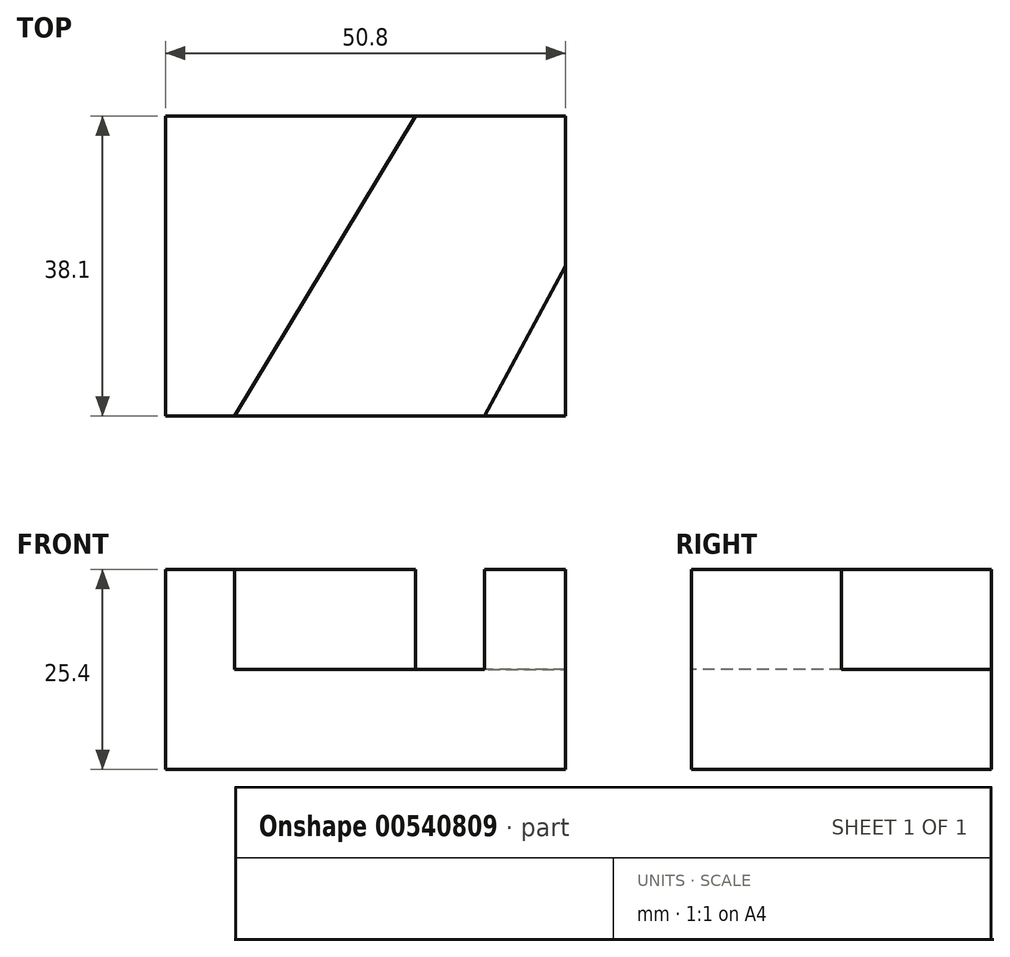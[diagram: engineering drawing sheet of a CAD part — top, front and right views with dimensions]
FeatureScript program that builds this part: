
annotation { "Feature Type Name" : "Feature", "Feature Type Description" : "" }
export const myFeature = defineFeature(function(context is Context, id is Id, definition is map)
    precondition{}
    {
        {
            var Q0;
            Q0=qCreatedBy(makeId("Front.planeOp"),FACE);
            var sketch = newSketch(context, id + "F0", { "sketchPlane" : qUnion([Q0])});
            skLineSegment(sketch, "E0", {"start": v(0, 0) * mm, "end": v(0, 25.4) * mm});
            skLineSegment(sketch, "E1", {"start": v(0, 25.4) * mm, "end": v(50.8, 25.4) * mm});
            skLineSegment(sketch, "E2", {"start": v(50.8, 25.4) * mm, "end": v(50.8, 0) * mm});
            skLineSegment(sketch, "E3", {"start": v(50.8, 0) * mm, "end": v(0, 0) * mm});
            skSolve(sketch);
        }
        {
            var Q0;
            Q0=makeQuery(id+"F0.imprint","IMPRINT",FACE,{"disambiguationData":[TD([[makeQuery(id+"F0.imprint","IMPRINT",EDGE,{"derivedFrom":sQuery(id+"F0.wireOp",EDGE,"E0")}),-1.0]])]});
            extrude(context, id + "F1", {"entities" : qUnion([Q0]), "depth" : 38.1 * mm, "offsetDistance" : 25.4 * mm});
        }
        {
            var Q0;
            Q0=makeQuery(id+"F1.opExtrude","SWEPT_FACE",FACE,{"disambiguationData":[OSD([sQuery(id+"F0.wireOp",EDGE,"E1")])]});
            var sketch = newSketch(context, id + "F2", { "sketchPlane" : qUnion([Q0])});
            skLineSegment(sketch, "E4", {"start": v(50.8, -19.05) * mm, "end": v(40.52, -38.1) * mm});
            skLineSegment(sketch, "E5", {"start": v(40.52, -38.1) * mm, "end": v(50.8, -38.1) * mm});
            skLineSegment(sketch, "E6", {"start": v(50.8, -38.1) * mm, "end": v(50.8, -19.05) * mm});
            skSolve(sketch);
        }
        {
            var Q0;
            {var subQ3=sQuery(id+"F2.wireOp",EDGE,"E4");Q0=makeQuery(id+"F2.imprint","IMPRINT",FACE,{"disambiguationData":[TD([[makeQuery(id+"F2.imprint","IMPRINT",EDGE,{"derivedFrom":subQ3}),-1.0]])]});}
            var sketch = newSketch(context, id + "F3", { "sketchPlane" : qUnion([Q0])});
            skLineSegment(sketch, "E7", {"start": v(31.75, 0) * mm, "end": v(8.77, -38.1) * mm});
            skLineSegment(sketch, "E8", {"start": v(8.77, -38.1) * mm, "end": v(40.52, -38.1) * mm});
            skLineSegment(sketch, "E9", {"start": v(40.52, -38.1) * mm, "end": v(50.8, -19.05) * mm});
            skLineSegment(sketch, "E10", {"start": v(50.8, -19.05) * mm, "end": v(50.8, 0) * mm});
            skLineSegment(sketch, "E11", {"start": v(50.8, 0) * mm, "end": v(31.75, 0) * mm});
            skSolve(sketch);
        }
        {
            var Q0;
            Q0=makeQuery(id+"F3.imprint","IMPRINT",FACE,{"disambiguationData":[TD([[makeQuery(id+"F3.imprint","IMPRINT",EDGE,{"derivedFrom":sQuery(id+"F3.wireOp",EDGE,"E7")}),1.0]])]});
            extrude(context, id + "F4", {"entities" : qUnion([Q0]), "operationType" : NewBodyOperationType.REMOVE, "oppositeDirection" : true, "depth" : 12.7 * mm, "offsetDistance" : 25.4 * mm});
        }
    });
